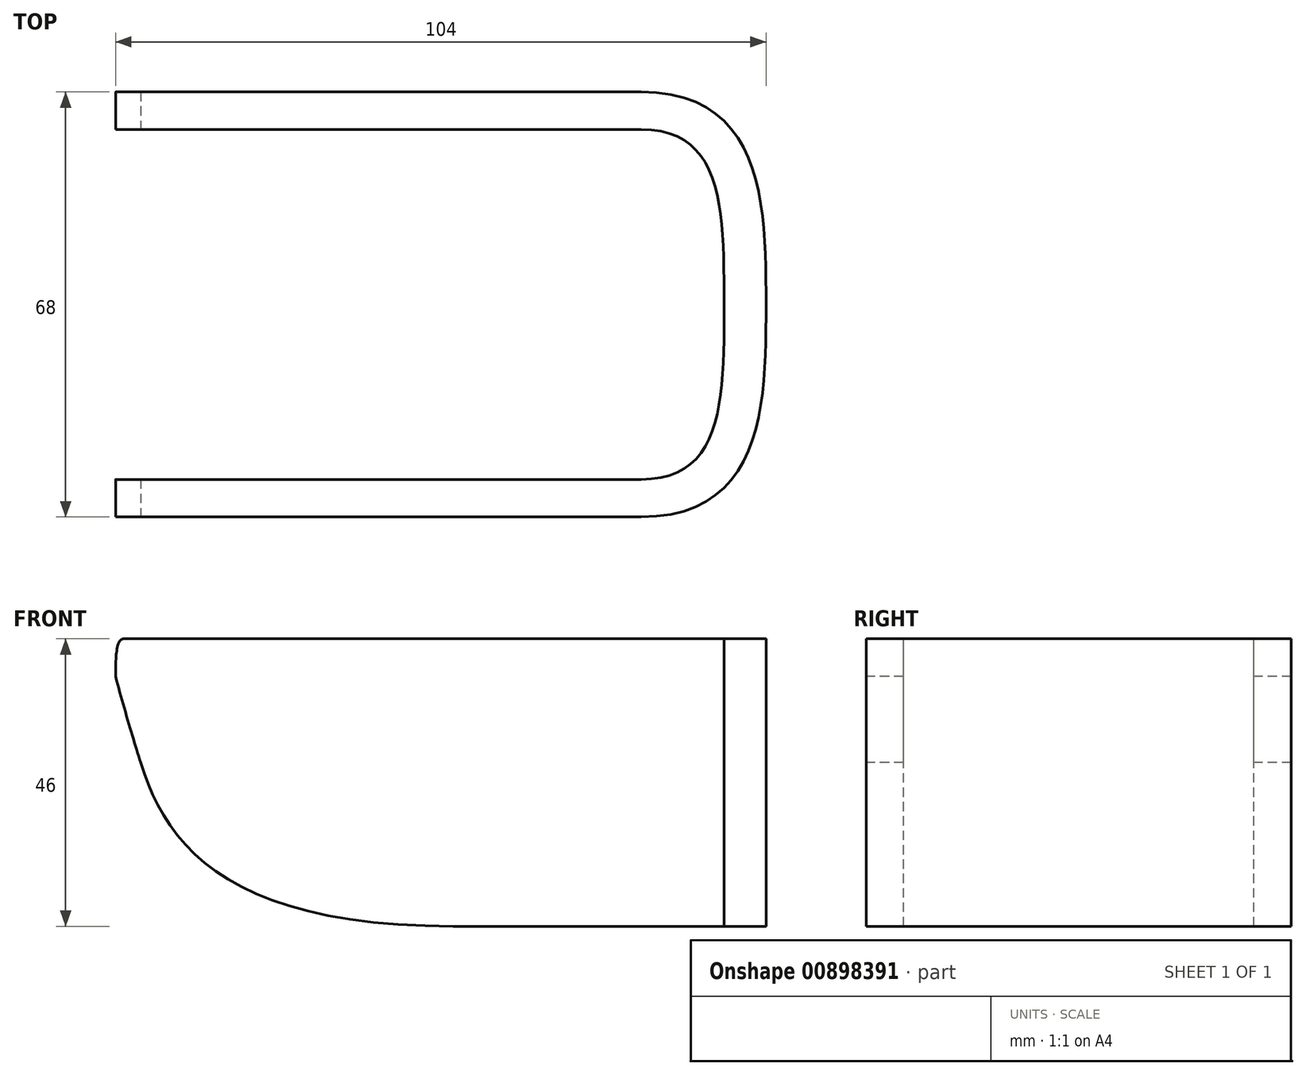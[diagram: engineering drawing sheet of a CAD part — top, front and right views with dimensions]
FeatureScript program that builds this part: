
annotation { "Feature Type Name" : "Feature", "Feature Type Description" : "" }
export const myFeature = defineFeature(function(context is Context, id is Id, definition is map)
    precondition{}
    {
        {
            var Q0;
            Q0=qCreatedBy(makeId("Front.planeOp"),FACE);
            var sketch = newSketch(context, id + "F0", { "sketchPlane" : qUnion([Q0])});
            skLineSegment(sketch, "E0.bottom", {"start": v(-47.53, 46) * mm, "end": v(56.47, 46) * mm});
            skLineSegment(sketch, "E0.top", {"start": v(-47.53, 0) * mm, "end": v(56.47, 0) * mm});
            skLineSegment(sketch, "E0.left", {"start": v(-47.53, 46) * mm, "end": v(-47.53, 0) * mm});
            skLineSegment(sketch, "E0.right", {"start": v(56.47, 46) * mm, "end": v(56.47, 0) * mm});
            skSolve(sketch);
        }
        {
            var Q0;
            Q0 = qSketchRegion(id + "F0", true);
            extrude(context, id + "F1", {"entities" : qUnion([Q0]), "endBound" : BoundingType.SYMMETRIC, "depth" : 68 * mm, "offsetDistance" : 25 * mm});
        }
        {
            var Q0;
            Q0=makeQuery(id+"F1.opExtrude","SWEPT_FACE",FACE,{"disambiguationData":[OSD([sQuery(id+"F0.wireOp",EDGE,"E0.bottom")])]});
            var sketch = newSketch(context, id + "F2", { "sketchPlane" : qUnion([Q0])});
            skFitSpline(sketch, "E1", {"points": [v(36.47, 34) * mm, v(56.47, 0) * mm], "startDerivative": vector(60, 0) * mm, "endDerivative": vector(0, -45) * mm});
            skFitSpline(sketch, "E2", {"points": [v(56.47, 0) * mm, v(36.47, -34) * mm], "startDerivative": vector(0, -45) * mm, "endDerivative": vector(-60, 0) * mm});
            skLineSegment(sketch, "E3", {"start": v(36.47, 34) * mm, "end": v(56.47, 34) * mm});
            skLineSegment(sketch, "E4", {"start": v(56.47, -34) * mm, "end": v(36.47, -34) * mm});
            skLineSegment(sketch, "E5", {"start": v(56.47, -34) * mm, "end": v(56.47, 34) * mm});
            skSolve(sketch);
        }
        {
            var Q0;
            Q0 = qSketchRegion(id + "F2", true);
            extrude(context, id + "F3", {"entities" : qUnion([Q0]), "operationType" : NewBodyOperationType.REMOVE, "endBound" : BoundingType.THROUGH_ALL, "oppositeDirection" : true, "depth" : 25 * mm, "offsetDistance" : 25 * mm});
        }
        {
            var Q0;
            Q0=makeQuery(id+"F1.opExtrude","SWEPT_FACE",FACE,{"disambiguationData":[OSD([sQuery(id+"F0.wireOp",EDGE,"E0.bottom")])]});
            var sketch = newSketch(context, id + "F4", { "sketchPlane" : qUnion([Q0])});
            skLineSegment(sketch, "E6.bottom", {"start": v(-47.53, 28) * mm, "end": v(36.47, 28) * mm});
            skLineSegment(sketch, "E6.top", {"start": v(-47.53, -28) * mm, "end": v(36.47, -28) * mm});
            skLineSegment(sketch, "E6.left", {"start": v(-47.53, 28) * mm, "end": v(-47.53, -28) * mm});
            skFitSpline(sketch, "E7", {"points": [v(36.47, 28) * mm, v(49.76, 0) * mm], "startDerivative": vector(39.86, 0) * mm, "endDerivative": vector(0.02, -45) * mm});
            skFitSpline(sketch, "E8", {"points": [v(49.76, 0) * mm, v(36.47, -28) * mm], "startDerivative": vector(0, -45) * mm, "endDerivative": vector(-39.88, 0) * mm});
            skSolve(sketch);
        }
        {
            var Q0;
            Q0 = qSketchRegion(id + "F4", true);
            extrude(context, id + "F5", {"entities" : qUnion([Q0]), "operationType" : NewBodyOperationType.REMOVE, "endBound" : BoundingType.THROUGH_ALL, "oppositeDirection" : true, "depth" : 25 * mm, "offsetDistance" : 25 * mm});
        }
        {
            var Q0;
            Q0=makeQuery(id+"F1.opExtrude","CAP_FACE",FACE,{"disambiguationData":[OSD([sQuery(id+"F0.wireOp",EDGE,"E0.bottom"),sQuery(id+"F0.wireOp",EDGE,"E0.top"),sQuery(id+"F0.wireOp",EDGE,"E0.left"),sQuery(id+"F0.wireOp",EDGE,"E0.right")])],"isStart":false});
            var sketch = newSketch(context, id + "F6", { "sketchPlane" : qUnion([Q0])});
            skFitSpline(sketch, "E9", {"points": [v(6.47, 0) * mm, v(-43.53, 26.2) * mm], "startDerivative": vector(-108, 0) * mm, "endDerivative": vector(-12, 39.6) * mm});
            skFitSpline(sketch, "E10", {"points": [v(-43.53, 26.2) * mm, v(-47.53, 40) * mm], "startDerivative": vector(-3.47, 10.94) * mm, "endDerivative": vector(-3.76, 14.34) * mm});
            skFitSpline(sketch, "E11", {"points": [v(-47.53, 40) * mm, v(-46.28, 46) * mm], "startDerivative": vector(0, 7.38) * mm, "endDerivative": vector(3.76, 0) * mm});
            skLineSegment(sketch, "E12", {"start": v(-46.28, 46) * mm, "end": v(-47.53, 46) * mm});
            skLineSegment(sketch, "E13", {"start": v(-47.53, 46) * mm, "end": v(-47.53, 0) * mm});
            skLineSegment(sketch, "E14", {"start": v(6.47, 0) * mm, "end": v(-47.53, 0) * mm});
            skSolve(sketch);
        }
        {
            var Q0;
            Q0 = qSketchRegion(id + "F6", true);
            extrude(context, id + "F7", {"entities" : qUnion([Q0]), "operationType" : NewBodyOperationType.REMOVE, "endBound" : BoundingType.THROUGH_ALL, "oppositeDirection" : true, "depth" : 25 * mm, "offsetDistance" : 25 * mm});
        }
    });
